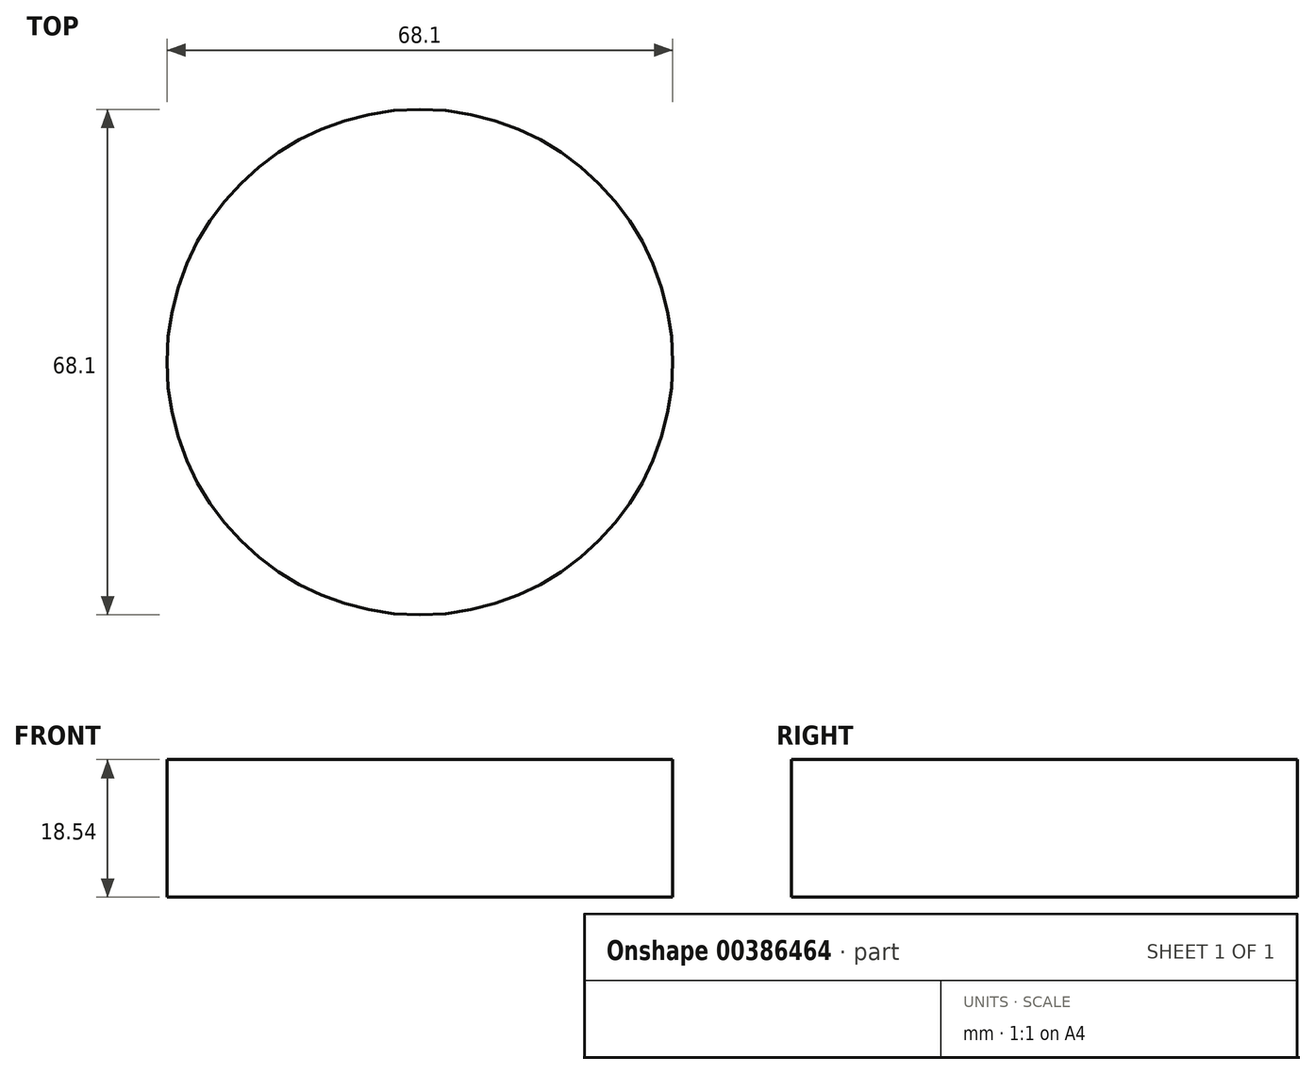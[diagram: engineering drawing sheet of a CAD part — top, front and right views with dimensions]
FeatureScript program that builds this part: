
annotation { "Feature Type Name" : "Feature", "Feature Type Description" : "" }
export const myFeature = defineFeature(function(context is Context, id is Id, definition is map)
    precondition{}
    {
        {
            var Q0;
            Q0=qCreatedBy(makeId("Top.planeOp"),FACE);
            var sketch = newSketch(context, id + "F0", { "sketchPlane" : qUnion([Q0])});
            skCircle(sketch, "E0", {"center": v(0, 0) * mm, "radius": 34.05 * mm});
            skSolve(sketch);
        }
        {
            var Q0;
            Q0=makeQuery(id+"F0.imprint","IMPRINT",FACE,{"disambiguationData":[TD([[makeQuery(id+"F0.imprint","IMPRINT",EDGE,{"derivedFrom":sQuery(id+"F0.wireOp",EDGE,"E0")}),1.0]])]});
            extrude(context, id + "F1", {"entities" : qUnion([Q0]), "depth" : 18.54 * mm});
        }
    });
